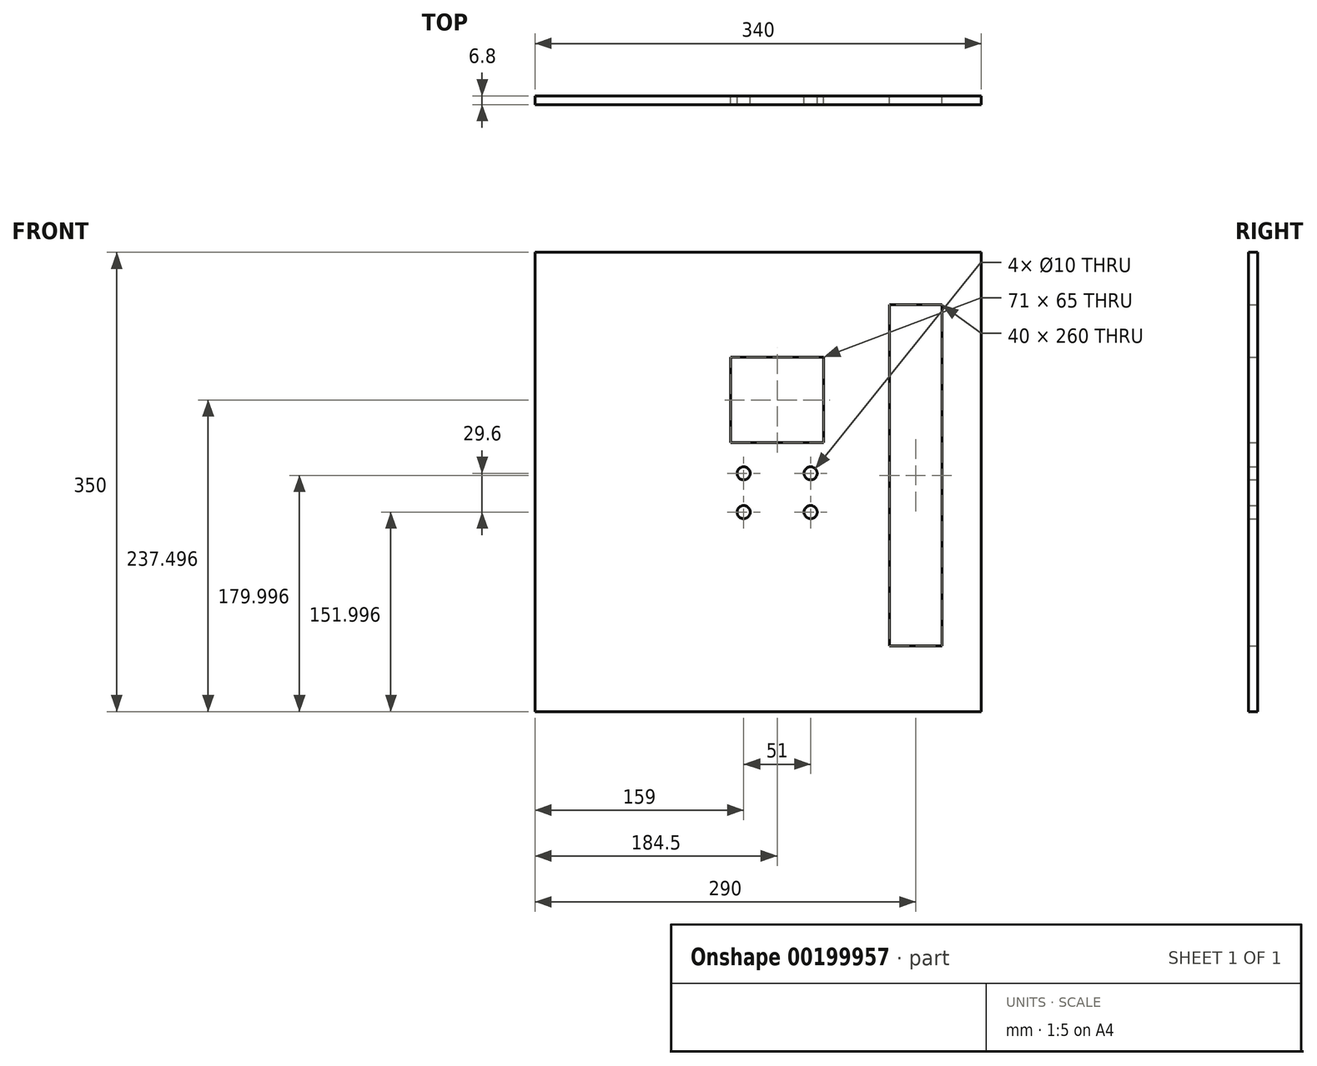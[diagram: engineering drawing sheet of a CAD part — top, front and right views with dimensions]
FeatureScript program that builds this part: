
annotation { "Feature Type Name" : "Feature", "Feature Type Description" : "" }
export const myFeature = defineFeature(function(context is Context, id is Id, definition is map)
    precondition{}
    {
        {
            var Q0;
            Q0=qCreatedBy(makeId("Front.planeOp"),FACE);
            var sketch = newSketch(context, id + "F0", { "sketchPlane" : qUnion([Q0])});
            skLineSegment(sketch, "E0.bottom", {"start": v(191, 253.24) * mm, "end": v(-149, 253.24) * mm});
            skLineSegment(sketch, "E0.top", {"start": v(191, -96.76) * mm, "end": v(-149, -96.76) * mm});
            skLineSegment(sketch, "E0.left", {"start": v(191, 253.24) * mm, "end": v(191, -96.76) * mm});
            skLineSegment(sketch, "E0.right", {"start": v(-149, 253.24) * mm, "end": v(-149, -96.76) * mm});
            skLineSegment(sketch, "E1.bottom", {"start": v(161, 213.24) * mm, "end": v(121, 213.24) * mm});
            skLineSegment(sketch, "E1.top", {"start": v(161, -46.76) * mm, "end": v(121, -46.76) * mm});
            skLineSegment(sketch, "E1.left", {"start": v(161, 213.24) * mm, "end": v(161, -46.76) * mm});
            skLineSegment(sketch, "E1.right", {"start": v(121, 213.24) * mm, "end": v(121, -46.76) * mm});
            skLineSegment(sketch, "E2.bottom", {"start": v(71, 173.24) * mm, "end": v(0, 173.24) * mm});
            skLineSegment(sketch, "E2.top", {"start": v(71, 108.24) * mm, "end": v(0, 108.24) * mm});
            skLineSegment(sketch, "E2.left", {"start": v(71, 173.24) * mm, "end": v(71, 108.24) * mm});
            skLineSegment(sketch, "E2.right", {"start": v(0, 173.24) * mm, "end": v(0, 108.24) * mm});
            skArc(sketch, "E3", {"start": v(15, 55.24) * mm, "mid": v(10, 60.24) * mm, "end": v(5, 55.24) * mm});
            skArc(sketch, "E4", {"start": v(5, 84.84) * mm, "mid": v(10, 79.84) * mm, "end": v(15, 84.84) * mm});
            skArc(sketch, "E5", {"start": v(66, 55.24) * mm, "mid": v(61, 60.24) * mm, "end": v(56, 55.24) * mm});
            skArc(sketch, "E6", {"start": v(56, 84.84) * mm, "mid": v(61, 79.84) * mm, "end": v(66, 84.84) * mm});
            skCircle(sketch, "E7", {"center": v(10, 55.24) * mm, "radius": 5 * mm});
            skCircle(sketch, "E8", {"center": v(10, 84.84) * mm, "radius": 5 * mm});
            skCircle(sketch, "E9", {"center": v(61, 84.84) * mm, "radius": 5 * mm});
            skCircle(sketch, "E10", {"center": v(61, 55.24) * mm, "radius": 5 * mm});
            skSolve(sketch);
        }
        {
            var Q0;
            Q0 = qSketchRegion(id + "F0", true);
            extrude(context, id + "F1", {"entities" : qUnion([Q0]), "depth" : 6.8 * mm});
        }
    });
